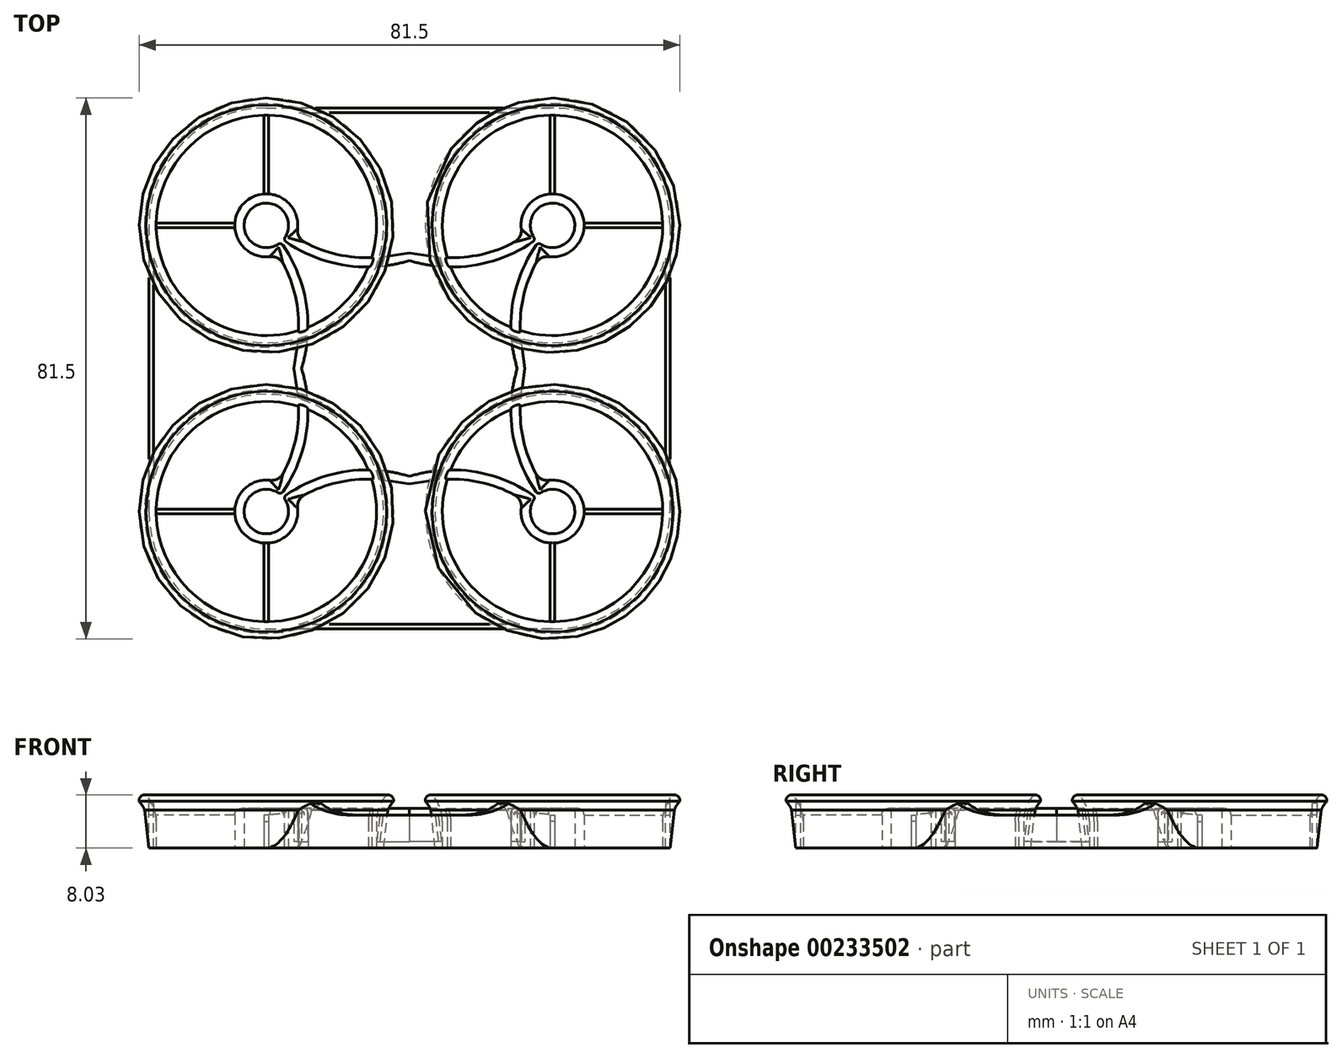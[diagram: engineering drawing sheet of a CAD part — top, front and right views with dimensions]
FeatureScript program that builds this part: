
annotation { "Feature Type Name" : "Feature", "Feature Type Description" : "" }
export const myFeature = defineFeature(function(context is Context, id is Id, definition is map)
    precondition{}
    {
        {
            var Q0;
            Q0=qCreatedBy(makeId("Top.planeOp"),FACE);
            var sketch = newSketch(context, id + "F0", { "sketchPlane" : qUnion([Q0])});
            skLineSegment(sketch, "E0", {"start": v(0, 0) * mm, "end": v(-6.72, 6.72) * mm, "construction": true});
            skLineSegment(sketch, "E1", {"start": v(-6.72, 6.72) * mm, "end": v(0, 13.44) * mm, "construction": true});
            skCircle(sketch, "E2", {"center": v(0, 13.44) * mm, "radius": 1 * mm});
            skLineSegment(sketch, "E3", {"start": v(0, 0) * mm, "end": v(-8.13, 8.13) * mm, "construction": true});
            skLineSegment(sketch, "E4", {"start": v(-8.13, 8.13) * mm, "end": v(0, 16.26) * mm, "construction": true});
            skLineSegment(sketch, "E5", {"start": v(0, 16.26) * mm, "end": v(-16.26, 0) * mm});
            skCircle(sketch, "E6.1.0", {"center": v(-13.44, 0) * mm, "radius": 1 * mm});
            skLineSegment(sketch, "E6.1.1", {"start": v(-16.26, 0) * mm, "end": v(0, -16.26) * mm});
            skCircle(sketch, "E6.2.0", {"center": v(0, -13.44) * mm, "radius": 1 * mm});
            skLineSegment(sketch, "E6.2.1", {"start": v(0, -16.26) * mm, "end": v(16.26, 0) * mm});
            skCircle(sketch, "E6.3.0", {"center": v(13.44, 0) * mm, "radius": 1 * mm});
            skLineSegment(sketch, "E6.3.1", {"start": v(16.26, 0) * mm, "end": v(0, 16.26) * mm});
            skPoint(sketch, "E6.center", {"position": v(0, 0) * mm});
            skLineSegment(sketch, "E7", {"start": v(0, 0) * mm, "end": v(-21.57, 21.57) * mm, "construction": true});
            skCircle(sketch, "E8", {"center": v(-21.57, 21.57) * mm, "radius": 15.5 * mm, "construction": true});
            skLineSegment(sketch, "E9.bottom", {"start": v(9.75, -11.5) * mm, "end": v(-9.75, -11.5) * mm, "construction": true});
            skLineSegment(sketch, "E9.top", {"start": v(9.75, 11.5) * mm, "end": v(-9.75, 11.5) * mm, "construction": true});
            skLineSegment(sketch, "E9.left", {"start": v(9.75, -11.5) * mm, "end": v(9.75, 11.5) * mm, "construction": true});
            skLineSegment(sketch, "E9.right", {"start": v(-9.75, -11.5) * mm, "end": v(-9.75, 11.5) * mm, "construction": true});
            skLineSegment(sketch, "E10", {"start": v(-21.57, 21.57) * mm, "end": v(0, 21.57) * mm});
            skCircle(sketch, "E11", {"center": v(-21.57, 21.57) * mm, "radius": 3.35 * mm});
            skCircle(sketch, "E12", {"center": v(-21.57, 21.57) * mm, "radius": 4.75 * mm});
            skArc(sketch, "E13", {"start": v(-19.02, 19.4) * mm, "mid": v(-9.88, 15.57) * mm, "end": v(0, 16.26) * mm});
            skArc(sketch, "E14.0", {"start": v(-18.35, 20.63) * mm, "mid": v(-11.33, 17.3) * mm, "end": v(-3.57, 16.89) * mm});
            skLineSegment(sketch, "E15", {"start": v(-3.57, 16.89) * mm, "end": v(0, 17.4) * mm});
            skArc(sketch, "E16.MirrorCS", {"start": v(-19.4, 19.02) * mm, "mid": v(-15.57, 9.88) * mm, "end": v(-16.26, 0) * mm});
            skArc(sketch, "E17.MirrorCS", {"start": v(-20.63, 18.35) * mm, "mid": v(-17.3, 11.33) * mm, "end": v(-16.89, 3.57) * mm});
            skLineSegment(sketch, "E18.MirrorCS", {"start": v(-16.89, 3.57) * mm, "end": v(-17.4, 0) * mm});
            skLineSegment(sketch, "E19", {"start": v(0, 17.4) * mm, "end": v(0, 16.26) * mm});
            skLineSegment(sketch, "E20", {"start": v(-17.4, 0) * mm, "end": v(-16.26, 0) * mm});
            skSolve(sketch);
        }
        {
            var Q0;
            Q0=sQuery(id+"F0.wireOp",EDGE,"E10");
            extrude(context, id + "F1", {"bodyType" : ToolBodyType.SURFACE, "surfaceEntities" : qUnion([Q0]), "depth" : 25 * mm});
        }
        {
            var Q0;
            Q0=makeQuery(id+"F1.opExtrude","SWEPT_FACE",FACE,{"disambiguationData":[OSD([sQuery(id+"F0.wireOp",EDGE,"E10")])]});
            var sketch = newSketch(context, id + "F2", { "sketchPlane" : qUnion([Q0])});
            skLineSegment(sketch, "E21", {"start": v(-4.97, 0) * mm, "end": v(-4.97, -1) * mm});
            skLineSegment(sketch, "E22", {"start": v(-4.97, -1) * mm, "end": v(-3.57, -1) * mm});
            skLineSegment(sketch, "E23", {"start": v(-3.57, -1) * mm, "end": v(-3.57, 3) * mm});
            skLineSegment(sketch, "E24", {"start": v(-4.97, 0) * mm, "end": v(-4.97, 3) * mm});
            skLineSegment(sketch, "E25", {"start": v(-4.97, 3) * mm, "end": v(1.03, 3) * mm, "construction": true});
            skArc(sketch, "E26", {"start": v(-4.97, 3) * mm, "mid": v(-4.57, 5.14) * mm, "end": v(-3.44, 7) * mm});
            skArc(sketch, "E27", {"start": v(-3.57, 3) * mm, "mid": v(-3.26, 4.64) * mm, "end": v(-2.4, 6.07) * mm});
            skArc(sketch, "E28", {"start": v(-2.4, 6.07) * mm, "mid": v(-2.67, 6.81) * mm, "end": v(-3.44, 7) * mm});
            skLineSegment(sketch, "E29", {"start": v(1.03, 3) * mm, "end": v(-3.44, 7) * mm, "construction": true});
            skSolve(sketch);
        }
        {
            var Q0;
            {var subQ0=sQuery(id+"F2.wireOp",EDGE,"E21");Q0=makeQuery(id+"F2.imprint","IMPRINT",FACE,{"disambiguationData":[TD([[makeQuery(id+"F2.imprint","IMPRINT",EDGE,{"derivedFrom":subQ0}),1.0]])]});}
            var Q1;
            {var subQ1=sQuery(id+"F2.wireOp",EDGE,"E24");Q1=makeQuery(id+"F2.imprint","IMPRINT",FACE,{"disambiguationData":[TD([[makeQuery(id+"F2.imprint","IMPRINT",EDGE,{"derivedFrom":subQ1}),-1.0]])]});}
            var Q2;
            Q2=makeQuery(id+"F1.opExtrude","SWEPT_EDGE",EDGE,{"disambiguationData":[OSD([sQuery(id+"F0.wireOp",VERTEX,"E10.start")])]});
            revolve(context, id + "F3", {"entities" : qUnion([Q0, Q1]), "axis" : qUnion([Q2]), "revolveType" : RevolveType.FULL});
        }
        {
            var Q0;
            Q0=makeQuery(id+"F3.opRevolve","SWEPT_EDGE",EDGE,{"disambiguationData":[OSD([sQuery(id+"F2.wireOp",EDGE,"E22"),sQuery(id+"F2.wireOp",EDGE,"E23")])]});
            chamfer(context, id + "F4", {"entities" : qUnion([Q0]), "chamferType" : ChamferType.TWO_OFFSETS, "width1" : 0.7 * mm, "oppositeDirection" : false, "width2" : 6 * mm, "tangentPropagation" : true});
        }
        {
            var Q0;
            {var subQ0=sQuery(id+"F0.wireOp",EDGE,"E12");var subQ1=sQuery(id+"F0.wireOp",EDGE,"E10");var subQ2=makeQuery(id+"F0.imprint","INTERSECT",VERTEX,{"derivedFrom":[subQ1,subQ0]});Q0=makeQuery(id+"F0.imprint","IMPRINT",FACE,{"disambiguationData":[TD([[makeQuery(id+"F0.imprint","IMPRINT",EDGE,{"disambiguationData":[TD([[subQ2,1.0]])],"derivedFrom":subQ1}),1.0]])]});}
            var Q1;
            {var subQ0=sQuery(id+"F0.wireOp",EDGE,"E12");var subQ1=sQuery(id+"F0.wireOp",EDGE,"E10");var subQ2=makeQuery(id+"F0.imprint","INTERSECT",VERTEX,{"derivedFrom":[subQ1,subQ0]});Q1=makeQuery(id+"F0.imprint","IMPRINT",FACE,{"disambiguationData":[TD([[makeQuery(id+"F0.imprint","IMPRINT",EDGE,{"disambiguationData":[TD([[subQ2,1.0]])],"derivedFrom":subQ1}),-1.0]])]});}
            var Q2;
            {var subQ0=sQuery(id+"F0.wireOp",EDGE,"E13");var subQ1=sQuery(id+"F0.wireOp",EDGE,"E11");var subQ2=makeQuery(id+"F0.imprint","INTERSECT",VERTEX,{"derivedFrom":[subQ1,subQ0]});Q2=makeQuery(id+"F0.imprint","IMPRINT",FACE,{"disambiguationData":[TD([[makeQuery(id+"F0.imprint","IMPRINT",EDGE,{"disambiguationData":[TD([[subQ2,-1.0]])],"derivedFrom":subQ1}),-1.0]])]});}
            var Q3;
            {var subQ0=sQuery(id+"F0.wireOp",EDGE,"E16.MirrorCS");var subQ1=sQuery(id+"F0.wireOp",EDGE,"E11");var subQ2=makeQuery(id+"F0.imprint","INTERSECT",VERTEX,{"derivedFrom":[subQ1,subQ0]});Q3=makeQuery(id+"F0.imprint","IMPRINT",FACE,{"disambiguationData":[TD([[makeQuery(id+"F0.imprint","IMPRINT",EDGE,{"disambiguationData":[TD([[subQ2,1.0]])],"derivedFrom":subQ1}),-1.0]])]});}
            var Q4;
            {var subQ4=sQuery(id+"F0.wireOp",EDGE,"E18.MirrorCS");Q4=makeQuery(id+"F0.imprint","IMPRINT",FACE,{"disambiguationData":[TD([[makeQuery(id+"F0.imprint","IMPRINT",EDGE,{"derivedFrom":subQ4}),1.0]])]});}
            var Q5;
            {var subQ0=sQuery(id+"F0.wireOp",EDGE,"E15");Q5=makeQuery(id+"F0.imprint","IMPRINT",FACE,{"disambiguationData":[TD([[makeQuery(id+"F0.imprint","IMPRINT",EDGE,{"derivedFrom":subQ0}),-1.0]])]});}
            extrude(context, id + "F5", {"entities" : qUnion([Q0, Q1, Q2, Q3, Q4, Q5]), "operationType" : NewBodyOperationType.ADD, "depth" : 5 * mm});
        }
        {
            var Q0;
            Q0=makeQuery(id+"F5.opExtrude","CAP_EDGE",EDGE,{"disambiguationData":[OSD([sQuery(id+"F0.wireOp",EDGE,"E12")])],"isStart":false});
            fillet(context, id + "F6", {"entities" : qUnion([Q0]), "radius" : 1 * mm, "tangentPropagation" : true, "allowEdgeOverflow" : false});
        }
        {
            var Q0;
            {var subQ0=sQuery(id+"F0.wireOp",EDGE,"E17.MirrorCS");Q0=makeQuery(id+"F5.boolean.opBoolean","SPLIT",EDGE,{"disambiguationData":[TD([makeQuery(id+"F3.opRevolve","SWEPT_FACE",FACE,{"disambiguationData":[OSD([sQuery(id+"F2.wireOp",EDGE,"E26")])]})])],"derivedFrom":makeQuery(id+"F5.opExtrude","CAP_EDGE",EDGE,{"disambiguationData":[OSD([subQ0])],"isStart":false})});}
            var Q1;
            {var subQ1=sQuery(id+"F0.wireOp",EDGE,"E16.MirrorCS");Q1=makeQuery(id+"F5.boolean.opBoolean","SPLIT",EDGE,{"disambiguationData":[TD([makeQuery(id+"F3.opRevolve","SWEPT_FACE",FACE,{"disambiguationData":[OSD([sQuery(id+"F2.wireOp",EDGE,"E26")])]})])],"derivedFrom":makeQuery(id+"F5.opExtrude","CAP_EDGE",EDGE,{"disambiguationData":[OSD([subQ1])],"isStart":false})});}
            var Q2;
            {var subQ1=sQuery(id+"F0.wireOp",EDGE,"E13");Q2=makeQuery(id+"F5.boolean.opBoolean","SPLIT",EDGE,{"disambiguationData":[TD([makeQuery(id+"F3.opRevolve","SWEPT_FACE",FACE,{"disambiguationData":[OSD([sQuery(id+"F2.wireOp",EDGE,"E26")])]})])],"derivedFrom":makeQuery(id+"F5.opExtrude","CAP_EDGE",EDGE,{"disambiguationData":[OSD([subQ1])],"isStart":false})});}
            var Q3;
            {var subQ0=sQuery(id+"F0.wireOp",EDGE,"E14.0");Q3=makeQuery(id+"F5.boolean.opBoolean","SPLIT",EDGE,{"disambiguationData":[TD([makeQuery(id+"F3.opRevolve","SWEPT_FACE",FACE,{"disambiguationData":[OSD([sQuery(id+"F2.wireOp",EDGE,"E26")])]})])],"derivedFrom":makeQuery(id+"F5.opExtrude","CAP_EDGE",EDGE,{"disambiguationData":[OSD([subQ0])],"isStart":false})});}
            fillet(context, id + "F7", {"entities" : qUnion([Q0, Q1, Q2, Q3]), "radius" : 0.7 * mm, "tangentPropagation" : true, "allowEdgeOverflow" : false});
        }
        {
            var Q0;
            Q0=makeQuery(id+"F5.opExtrude","SWEPT_EDGE",EDGE,{"disambiguationData":[OSD([sQuery(id+"F0.wireOp",EDGE,"E12"),sQuery(id+"F0.wireOp",EDGE,"E17.MirrorCS")])]});
            var Q1;
            Q1=makeQuery(id+"F5.opExtrude","SWEPT_EDGE",EDGE,{"disambiguationData":[OSD([sQuery(id+"F0.wireOp",EDGE,"E12"),sQuery(id+"F0.wireOp",EDGE,"E14.0")])]});
            fillet(context, id + "F8", {"entities" : qUnion([Q0, Q1]), "radius" : 2 * mm, "tangentPropagation" : true, "allowEdgeOverflow" : false});
        }
        {
            var Q0;
            {var subQ0=sQuery(id+"F0.wireOp",EDGE,"E12");var subQ1=sQuery(id+"F0.wireOp",EDGE,"E10");var subQ2=makeQuery(id+"F0.imprint","INTERSECT",VERTEX,{"derivedFrom":[subQ1,subQ0]});Q0=makeQuery(id+"F0.imprint","IMPRINT",FACE,{"disambiguationData":[TD([[makeQuery(id+"F0.imprint","IMPRINT",EDGE,{"disambiguationData":[TD([[subQ2,1.0]])],"derivedFrom":subQ1}),1.0]])]});}
            var Q1;
            {var subQ0=sQuery(id+"F0.wireOp",EDGE,"E16.MirrorCS");var subQ1=sQuery(id+"F0.wireOp",EDGE,"E11");var subQ2=makeQuery(id+"F0.imprint","INTERSECT",VERTEX,{"derivedFrom":[subQ1,subQ0]});Q1=makeQuery(id+"F0.imprint","IMPRINT",FACE,{"disambiguationData":[TD([[makeQuery(id+"F0.imprint","IMPRINT",EDGE,{"disambiguationData":[TD([[subQ2,1.0]])],"derivedFrom":subQ1}),-1.0]])]});}
            var Q2;
            {var subQ0=sQuery(id+"F0.wireOp",EDGE,"E12");var subQ1=sQuery(id+"F0.wireOp",EDGE,"E10");var subQ2=makeQuery(id+"F0.imprint","INTERSECT",VERTEX,{"derivedFrom":[subQ1,subQ0]});Q2=makeQuery(id+"F0.imprint","IMPRINT",FACE,{"disambiguationData":[TD([[makeQuery(id+"F0.imprint","IMPRINT",EDGE,{"disambiguationData":[TD([[subQ2,1.0]])],"derivedFrom":subQ1}),-1.0]])]});}
            var Q3;
            {var subQ0=sQuery(id+"F0.wireOp",EDGE,"E13");var subQ1=sQuery(id+"F0.wireOp",EDGE,"E11");var subQ2=makeQuery(id+"F0.imprint","INTERSECT",VERTEX,{"derivedFrom":[subQ1,subQ0]});Q3=makeQuery(id+"F0.imprint","IMPRINT",FACE,{"disambiguationData":[TD([[makeQuery(id+"F0.imprint","IMPRINT",EDGE,{"disambiguationData":[TD([[subQ2,-1.0]])],"derivedFrom":subQ1}),-1.0]])]});}
            var Q4;
            {var subQ0=sQuery(id+"F0.wireOp",EDGE,"E12");var subQ1=sQuery(id+"F0.wireOp",EDGE,"E13");var subQ2=sQuery(id+"F0.wireOp",EDGE,"E11");var subQ3=sQuery(id+"F0.wireOp",EDGE,"E16.MirrorCS");var subQ4=sQuery(id+"F0.wireOp",EDGE,"E14.0");var subQ5=sQuery(id+"F0.wireOp",EDGE,"E17.MirrorCS");Q4=makeQuery(id+"F5.boolean.opBoolean","SPLIT",FACE,{"disambiguationData":[TD([makeQuery(id+"F5.opExtrude","SWEPT_FACE",FACE,{"disambiguationData":[OSD([subQ2])]})])],"derivedFrom":makeQuery(id+"F5.opExtrude","CAP_FACE",FACE,{"disambiguationData":[OSD([subQ2,subQ0,subQ1,subQ4,sQuery(id+"F0.wireOp",EDGE,"E15"),subQ3,subQ5,sQuery(id+"F0.wireOp",EDGE,"E18.MirrorCS"),sQuery(id+"F0.wireOp",EDGE,"E19"),sQuery(id+"F0.wireOp",EDGE,"E20")])],"isStart":true})});}
            extrude(context, id + "F9", {"entities" : qUnion([Q0, Q1, Q2, Q3, Q4]), "operationType" : NewBodyOperationType.ADD, "oppositeDirection" : true, "depth" : 1 * mm});
        }
        {
            var Q0;
            Q0=makeQuery(id+"F5.opExtrude","SWEPT_EDGE",EDGE,{"disambiguationData":[OSD([sQuery(id+"F0.wireOp",EDGE,"E11"),sQuery(id+"F0.wireOp",EDGE,"E13")])]});
            var Q1;
            Q1=makeQuery(id+"F5.opExtrude","SWEPT_EDGE",EDGE,{"disambiguationData":[OSD([sQuery(id+"F0.wireOp",EDGE,"E11"),sQuery(id+"F0.wireOp",EDGE,"E16.MirrorCS")])]});
            fillet(context, id + "F10", {"entities" : qUnion([Q0, Q1]), "radius" : 0.5 * mm, "allowEdgeOverflow" : false});
        }
        {
            var Q0;
            Q0=makeQuery(id+"F9.opExtrude","CAP_FACE",FACE,{"disambiguationData":[OSD([sQuery(id+"F0.wireOp",EDGE,"E11"),sQuery(id+"F0.wireOp",EDGE,"E12"),sQuery(id+"F0.wireOp",EDGE,"E13"),sQuery(id+"F0.wireOp",EDGE,"E16.MirrorCS")])],"isStart":false});
            var sketch = newSketch(context, id + "F11", { "sketchPlane" : qUnion([Q0])});
            skLineSegment(sketch, "E30", {"start": v(-21.57, -21.57) * mm, "end": v(-21.57, -39.26) * mm, "construction": true});
            skLineSegment(sketch, "E31", {"start": v(-21.57, -21.57) * mm, "end": v(-39.26, -21.57) * mm, "construction": true});
            skLineSegment(sketch, "E32", {"start": v(-21.22, -26.3) * mm, "end": v(-21.22, -39.26) * mm});
            skLineSegment(sketch, "E33", {"start": v(-21.92, -26.3) * mm, "end": v(-21.92, -39.26) * mm});
            skLineSegment(sketch, "E34", {"start": v(-26.3, -21.92) * mm, "end": v(-39.26, -21.92) * mm});
            skLineSegment(sketch, "E35", {"start": v(-26.3, -21.22) * mm, "end": v(-39.26, -21.22) * mm});
            skLineSegment(sketch, "E36.bottom", {"start": v(-39.26, -21.57) * mm, "end": v(-38.56, -21.57) * mm});
            skLineSegment(sketch, "E36.top", {"start": v(-39.26, 0) * mm, "end": v(-38.56, 0) * mm});
            skLineSegment(sketch, "E36.left", {"start": v(-39.26, -21.57) * mm, "end": v(-39.26, 0) * mm});
            skLineSegment(sketch, "E36.right", {"start": v(-38.56, -21.57) * mm, "end": v(-38.56, 0) * mm});
            skLineSegment(sketch, "E37.bottom", {"start": v(-21.57, -39.26) * mm, "end": v(0, -39.26) * mm});
            skLineSegment(sketch, "E37.top", {"start": v(-21.57, -38.56) * mm, "end": v(0, -38.56) * mm});
            skLineSegment(sketch, "E37.left", {"start": v(-21.57, -39.26) * mm, "end": v(-21.57, -38.56) * mm});
            skLineSegment(sketch, "E37.right", {"start": v(0, -39.26) * mm, "end": v(0, -38.56) * mm});
            skArc(sketch, "E38", {"start": v(-39.26, -21.22) * mm, "mid": v(-39.26, -21.57) * mm, "end": v(-39.26, -21.92) * mm});
            skArc(sketch, "E39", {"start": v(-21.92, -39.26) * mm, "mid": v(-21.57, -39.26) * mm, "end": v(-21.22, -39.26) * mm});
            skSolve(sketch);
        }
        {
            var Q0;
            {var subQ1=sQuery(id+"F11.wireOp",EDGE,"E33");Q0=makeQuery(id+"F11.imprint","IMPRINT",FACE,{"disambiguationData":[TD([[makeQuery(id+"F11.imprint","IMPRINT",EDGE,{"derivedFrom":subQ1}),1.0]])]});}
            var Q1;
            {var subQ4=sQuery(id+"F11.wireOp",EDGE,"E34");Q1=makeQuery(id+"F11.imprint","IMPRINT",FACE,{"disambiguationData":[TD([[makeQuery(id+"F11.imprint","IMPRINT",EDGE,{"derivedFrom":subQ4}),-1.0]])]});}
            var Q2;
            {var subQ1=sQuery(id+"F11.wireOp",EDGE,"E36.top");Q2=makeQuery(id+"F11.imprint","IMPRINT",FACE,{"disambiguationData":[TD([[makeQuery(id+"F11.imprint","IMPRINT",EDGE,{"derivedFrom":subQ1}),-1.0]])]});}
            var Q3;
            {var subQ1=sQuery(id+"F11.wireOp",EDGE,"E37.bottom");Q3=makeQuery(id+"F11.imprint","IMPRINT",FACE,{"disambiguationData":[TD([[makeQuery(id+"F11.imprint","IMPRINT",EDGE,{"derivedFrom":subQ1}),1.0]])]});}
            extrude(context, id + "F12", {"entities" : qUnion([Q0, Q1, Q2, Q3]), "operationType" : NewBodyOperationType.ADD, "oppositeDirection" : true, "depth" : 5 * mm});
        }
        {
            var Q0;
            Q0=makeQuery(id+"F12.boolean.opBoolean","INTERSECT",EDGE,{"derivedFrom":[makeQuery(id+"F4.opChamfer","BLEND_FACE",FACE,{"disambiguationData":[OSD([sQuery(id+"F2.wireOp",EDGE,"E22"),sQuery(id+"F2.wireOp",EDGE,"E23")])]}),makeQuery(id+"F12.opExtrude","CAP_FACE",FACE,{"disambiguationData":[OSD([sQuery(id+"F11.wireOp",EDGE,"E35"),sQuery(id+"F11.wireOp",EDGE,"E36.top"),sQuery(id+"F11.wireOp",EDGE,"E36.left"),sQuery(id+"F11.wireOp",EDGE,"E36.right"),sQuery(id+"F11.wireOp",EDGE,"E38")])],"isStart":false})]});
            var Q1;
            Q1=makeQuery(id+"F12.boolean.opBoolean","INTERSECT",EDGE,{"derivedFrom":[makeQuery(id+"F4.opChamfer","BLEND_FACE",FACE,{"disambiguationData":[OSD([sQuery(id+"F2.wireOp",EDGE,"E22"),sQuery(id+"F2.wireOp",EDGE,"E23")])]}),makeQuery(id+"F12.opExtrude","CAP_FACE",FACE,{"disambiguationData":[OSD([sQuery(id+"F11.wireOp",EDGE,"E32"),sQuery(id+"F11.wireOp",EDGE,"E37.bottom"),sQuery(id+"F11.wireOp",EDGE,"E37.top"),sQuery(id+"F11.wireOp",EDGE,"E37.right"),sQuery(id+"F11.wireOp",EDGE,"E39")])],"isStart":false})]});
            fillet(context, id + "F13", {"entities" : qUnion([Q0, Q1]), "radius" : 3 * mm, "tangentPropagation" : true, "allowEdgeOverflow" : false});
        }
        {
            var Q0;
            Q0=makeQuery(id+"F3.opRevolve","SWEPT_BODY",BODY,{"disambiguationData":[OSD([sQuery(id+"F2.wireOp",EDGE,"E21"),sQuery(id+"F2.wireOp",EDGE,"E22"),sQuery(id+"F2.wireOp",EDGE,"E23"),sQuery(id+"F2.wireOp",EDGE,"E24"),sQuery(id+"F2.wireOp",EDGE,"E26"),sQuery(id+"F2.wireOp",EDGE,"E27"),sQuery(id+"F2.wireOp",EDGE,"E28")])]});
            var Q1;
            Q1=qCreatedBy(makeId("Front.planeOp"),FACE);
            mirror(context, id + "F14", {"operationType" : NewBodyOperationType.ADD, "entities" : qUnion([Q0]), "mirrorPlane" : qUnion([Q1])});
        }
        {
            var Q0;
            Q0=makeQuery(id+"F3.opRevolve","SWEPT_BODY",BODY,{"disambiguationData":[OSD([sQuery(id+"F2.wireOp",EDGE,"E21"),sQuery(id+"F2.wireOp",EDGE,"E22"),sQuery(id+"F2.wireOp",EDGE,"E23"),sQuery(id+"F2.wireOp",EDGE,"E24"),sQuery(id+"F2.wireOp",EDGE,"E26"),sQuery(id+"F2.wireOp",EDGE,"E27"),sQuery(id+"F2.wireOp",EDGE,"E28")])]});
            var Q1;
            Q1=qCreatedBy(makeId("Right.planeOp"),FACE);
            mirror(context, id + "F15", {"operationType" : NewBodyOperationType.ADD, "entities" : qUnion([Q0]), "mirrorPlane" : qUnion([Q1])});
        }
    });
